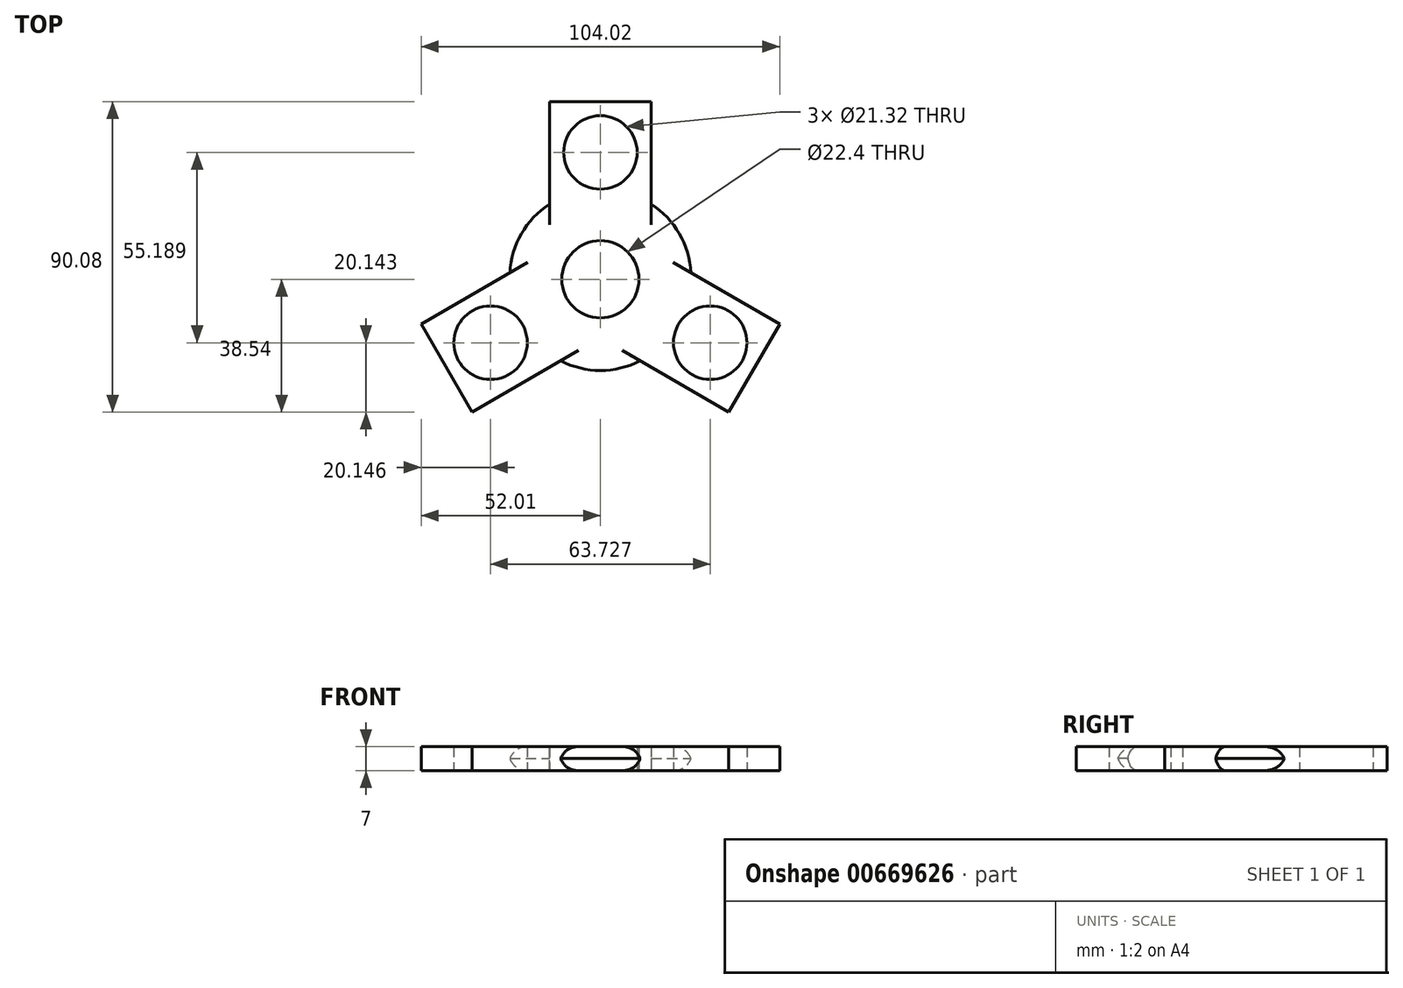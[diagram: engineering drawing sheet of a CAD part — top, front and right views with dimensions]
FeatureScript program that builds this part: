
annotation { "Feature Type Name" : "Feature", "Feature Type Description" : "" }
export const myFeature = defineFeature(function(context is Context, id is Id, definition is map)
    precondition{}
    {
        {
            var Q0;
            Q0=qCreatedBy(makeId("Top.planeOp"),FACE);
            var sketch = newSketch(context, id + "F0", { "sketchPlane" : qUnion([Q0])});
            skCircle(sketch, "E0", {"center": v(0, 0) * mm, "radius": 11.2 * mm});
            skCircle(sketch, "E1", {"center": v(0, 0) * mm, "radius": 13.2 * mm});
            skCircle(sketch, "E2", {"center": v(0, 36.8) * mm, "radius": 10.66 * mm});
            skCircle(sketch, "E3.cCircle", {"center": v(0, 36.8) * mm, "radius": 14.75 * mm, "construction": true});
            skLineSegment(sketch, "E3.0", {"start": v(-14.75, 51.54) * mm, "end": v(14.75, 51.54) * mm});
            skLineSegment(sketch, "E3.1", {"start": v(14.75, 51.54) * mm, "end": v(14.75, 22.05) * mm});
            skLineSegment(sketch, "E3.2", {"start": v(14.75, 22.05) * mm, "end": v(-14.75, 22.05) * mm});
            skLineSegment(sketch, "E3.3", {"start": v(-14.75, 22.05) * mm, "end": v(-14.75, 51.54) * mm});
            skPoint(sketch, "E3.0.midPoint", {"position": v(0, 51.54) * mm});
            skCircle(sketch, "E4.1.0", {"center": v(-31.86, -18.4) * mm, "radius": 14.75 * mm, "construction": true});
            skLineSegment(sketch, "E4.1.1", {"start": v(-52, -13) * mm, "end": v(-26.47, 1.75) * mm});
            skLineSegment(sketch, "E4.1.2", {"start": v(-37.26, -38.54) * mm, "end": v(-52, -13) * mm});
            skLineSegment(sketch, "E4.1.3", {"start": v(-11.72, -23.8) * mm, "end": v(-37.26, -38.54) * mm});
            skLineSegment(sketch, "E4.1.4", {"start": v(-26.47, 1.75) * mm, "end": v(-11.72, -23.8) * mm});
            skCircle(sketch, "E4.1.5", {"center": v(-31.86, -18.4) * mm, "radius": 10.66 * mm});
            skCircle(sketch, "E4.2.0", {"center": v(31.86, -18.4) * mm, "radius": 14.75 * mm, "construction": true});
            skLineSegment(sketch, "E4.2.1", {"start": v(37.26, -38.54) * mm, "end": v(11.72, -23.8) * mm});
            skLineSegment(sketch, "E4.2.2", {"start": v(52, -13) * mm, "end": v(37.26, -38.54) * mm});
            skLineSegment(sketch, "E4.2.3", {"start": v(26.47, 1.75) * mm, "end": v(52, -13) * mm});
            skLineSegment(sketch, "E4.2.4", {"start": v(11.72, -23.8) * mm, "end": v(26.47, 1.75) * mm});
            skCircle(sketch, "E4.2.5", {"center": v(31.86, -18.4) * mm, "radius": 10.66 * mm});
            skArc(sketch, "E5", {"start": v(-14.75, 22.05) * mm, "mid": v(-23.12, 13.35) * mm, "end": v(-26.47, 1.75) * mm});
            skArc(sketch, "E6.1.0", {"start": v(-11.72, -23.8) * mm, "mid": v(0, -26.7) * mm, "end": v(11.72, -23.8) * mm});
            skArc(sketch, "E6.2.0", {"start": v(26.47, 1.75) * mm, "mid": v(23.12, 13.35) * mm, "end": v(14.75, 22.05) * mm});
            skSolve(sketch);
        }
        {
            var Q0;
            Q0=makeQuery(id+"F0.imprint","IMPRINT",FACE,{"disambiguationData":[TD([[makeQuery(id+"F0.imprint","IMPRINT",EDGE,{"derivedFrom":sQuery(id+"F0.wireOp",EDGE,"E2")}),-1.0]])]});
            var Q1;
            Q1=makeQuery(id+"F0.imprint","IMPRINT",FACE,{"disambiguationData":[TD([[makeQuery(id+"F0.imprint","IMPRINT",EDGE,{"derivedFrom":sQuery(id+"F0.wireOp",EDGE,"E1")}),-1.0]])]});
            var Q2;
            Q2=makeQuery(id+"F0.imprint","IMPRINT",FACE,{"disambiguationData":[TD([[makeQuery(id+"F0.imprint","IMPRINT",EDGE,{"derivedFrom":sQuery(id+"F0.wireOp",EDGE,"E4.2.1")}),-1.0]])]});
            var Q3;
            Q3=makeQuery(id+"F0.imprint","IMPRINT",FACE,{"disambiguationData":[TD([[makeQuery(id+"F0.imprint","IMPRINT",EDGE,{"derivedFrom":sQuery(id+"F0.wireOp",EDGE,"E4.1.1")}),-1.0]])]});
            var Q4;
            Q4=makeQuery(id+"F0.imprint","IMPRINT",FACE,{"disambiguationData":[TD([[makeQuery(id+"F0.imprint","IMPRINT",EDGE,{"derivedFrom":sQuery(id+"F0.wireOp",EDGE,"E0")}),-1.0]])]});
            extrude(context, id + "F1", {"entities" : qUnion([Q0, Q1, Q2, Q3, Q4]), "depth" : 7 * mm, "offsetDistance" : 25 * mm});
        }
        {
            var Q0;
            Q0=makeQuery(id+"F1.opExtrude","CAP_EDGE",EDGE,{"disambiguationData":[OSD([sQuery(id+"F0.wireOp",EDGE,"E5")])],"isStart":false});
            var Q1;
            Q1=makeQuery(id+"F1.opExtrude","CAP_EDGE",EDGE,{"disambiguationData":[OSD([sQuery(id+"F0.wireOp",EDGE,"E6.2.0")])],"isStart":false});
            var Q2;
            Q2=makeQuery(id+"F1.opExtrude","CAP_EDGE",EDGE,{"disambiguationData":[OSD([sQuery(id+"F0.wireOp",EDGE,"E6.1.0")])],"isStart":false});
            var Q3;
            Q3=makeQuery(id+"F1.opExtrude","CAP_EDGE",EDGE,{"disambiguationData":[OSD([sQuery(id+"F0.wireOp",EDGE,"E6.2.0")])],"isStart":true});
            var Q4;
            Q4=makeQuery(id+"F1.opExtrude","CAP_EDGE",EDGE,{"disambiguationData":[OSD([sQuery(id+"F0.wireOp",EDGE,"E6.1.0")])],"isStart":true});
            var Q5;
            Q5=makeQuery(id+"F1.opExtrude","CAP_EDGE",EDGE,{"disambiguationData":[OSD([sQuery(id+"F0.wireOp",EDGE,"E5")])],"isStart":true});
            fillet(context, id + "F2", {"entities" : qUnion([Q0, Q1, Q2, Q3, Q4, Q5]), "radius" : 5 * mm, "tangentPropagation" : true, "allowEdgeOverflow" : false});
        }
    });
